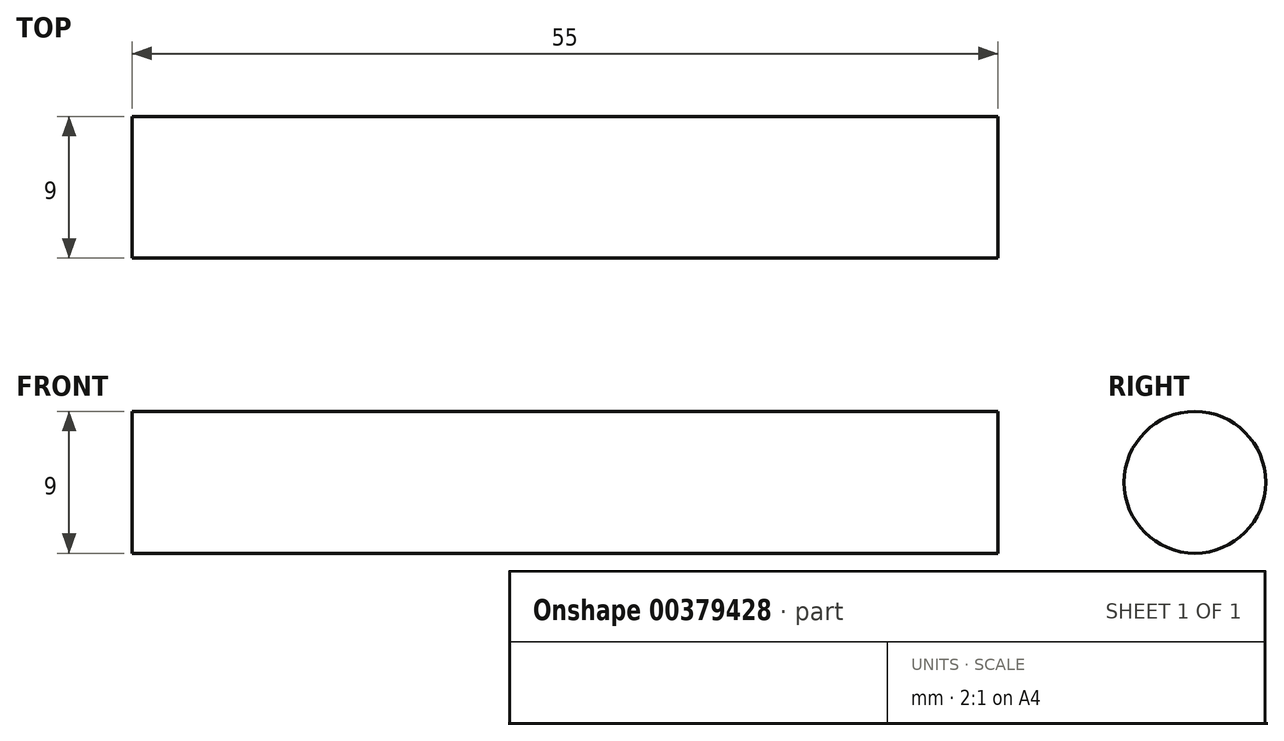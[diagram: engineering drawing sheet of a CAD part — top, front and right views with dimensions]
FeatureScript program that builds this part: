
annotation { "Feature Type Name" : "Feature", "Feature Type Description" : "" }
export const myFeature = defineFeature(function(context is Context, id is Id, definition is map)
    precondition{}
    {
        {
            var Q0;
            Q0=qCreatedBy(makeId("Right.planeOp"),FACE);
            var sketch = newSketch(context, id + "F0", { "sketchPlane" : qUnion([Q0])});
            skCircle(sketch, "E0", {"center": v(0, 0) * mm, "radius": 4.5 * mm});
            skSolve(sketch);
        }
        {
            var Q0;
            Q0=makeQuery(id+"F0.imprint","IMPRINT",FACE,{"disambiguationData":[TD([[makeQuery(id+"F0.imprint","IMPRINT",EDGE,{"derivedFrom":sQuery(id+"F0.wireOp",EDGE,"E0")}),1.0]])]});
            extrude(context, id + "F1", {"entities" : qUnion([Q0]), "depth" : 55 * mm});
        }
    });
